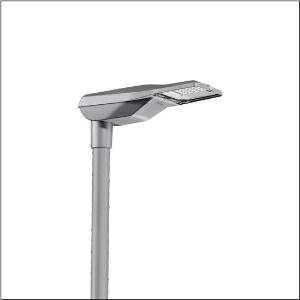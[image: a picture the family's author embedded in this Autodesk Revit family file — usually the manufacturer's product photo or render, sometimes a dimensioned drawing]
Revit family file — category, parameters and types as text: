
# Revit family: streetlight_sl_21_iq_micro___st0_8a_5xe1c31g08cb_6ed2
name_source: partatom
category: Lighting Fixtures
units: mm (PartAtom-declared; Revit-internal decimal feet)

## family parameters
Cut with Voids When Loaded = No
Host = Face
Light Source = No
Part Type = Normal
Room Calculation Point = No
Round Connector Dimension = Use Diameter
Shared = No

## types (1)
- --- (1 x LED, 2870 lm, 19.4 W, 3000K)
    Apparent Load = 19 VA
    CIE Flux Codes = 38 75 97 100 100
    Color Rendering = 70
    Color Temperature = 3000K
    Default Elevation = 1800 mm
    Description = Streetlight SL 21 iQ micro, mast luminaire, primary light control with lens, of PMMA, primary optical cover: cover, of toughened safety glass, transparent, light distribution: ST0.8a, light emission: direct distribution, primary light characteristic: asymmetric, installation type: post-top, side-entry, LED, High Power LED, rated luminous flux: 2.870lm, luminous efficacy: 148lm/W, light colour: 730, colour temperature: 3000K, control: Street-Remote, Auto-Match, Temp-Guard, Lumen-Switch, Night-Set, Smart-Wire, Light-Fading, Desk-Remote (wireless, voltage-free reading and setting of iQ features in the workshop via application-optimized NFC function/RFID function), optimised constant luminous flux control (CLO 2.0), presetting dimming linear, mains connection: 220..240V, AC, 50/60Hz, start of lifetime: 19W, end of service life: 20W, reduction: 10W, luminaire housing, of diecast aluminium, powder-coated, Siteco® metallic grey (DB 702S), corrosivity category C5 mid according to DIN EN ISO 12944, please order mast flange separately, inclination adjustable: 0°, 5°, 10°, 15°, sealing non-destructively replaceable, multi-level sealing system, length: 528mm, width: 235mm, height: 110mm, mast flange for spigot size: 42mm (side-entry): 5XC10008XM4, 60/48mm (side-entry/post-top): 5XC10108XM2, 76/60mm (side-entry/post-top): 5XC10108XM1, protection rating (complete): IP66, insulation class (complete): insulation class II (safety insulation), certification: CE, ENEC, ENEC+, VDE, impact resistance: IK09, permissible operating ambient temperature for outdoor applications: -40..+50°C, standard-compliant lighting for roads and squares, packaging unit: 1 piece

Light Distribution: ST0.8a
    Height = 110 mm
    Lamp = 1 x LED
    Lamp Light Flux = 2870 lm
    Lamp Power = 19.4 W
    Lamp count = 1
    Length = 528 mm
    Luminous efficacy = 148 lm/W
    Manufacturer = Siteco
    ModVariant = No
    Model = 5XE1C31G08CB
    Number of Poles = 1
    OnlyDefault = Yes
    Power Factor = 1
    Product Name = Streetlight SL 21 iQ micro | ST0.8a
    Product group = mast luminaire | pylon top
    ProductGroupID = 6100
    Protection Class = Protection class II
    Protection Degree = IP 66
    RLX_Detail_Level = 1
    RLX_Emergency_Light_Flux = 0 lm
    RLX_Emergency_Type = 0
    RLX_Emergency_Type_DB = No
    RlxData = <blob elided: 98613 chars, md5=be578eda>
    Socket = socket
    Standby Power = 0 W
    System Light Flux = 2870 lm
    System Power = 19 W
    Type Comments = factory setting: luminous flux: 100 % | dim-lin: 254 | 387 mA
    Type Image = l_1006881.jpg
    URL = http://relux.com
    VarID = @adj_069753
    Voltage = 0 V
    Weight = 0.00 kg
    Width = 235 mm

## geometry (parser evidence)
native form markers: Blend x4, Sweep x12
no freeform markers — native parametric forms only
